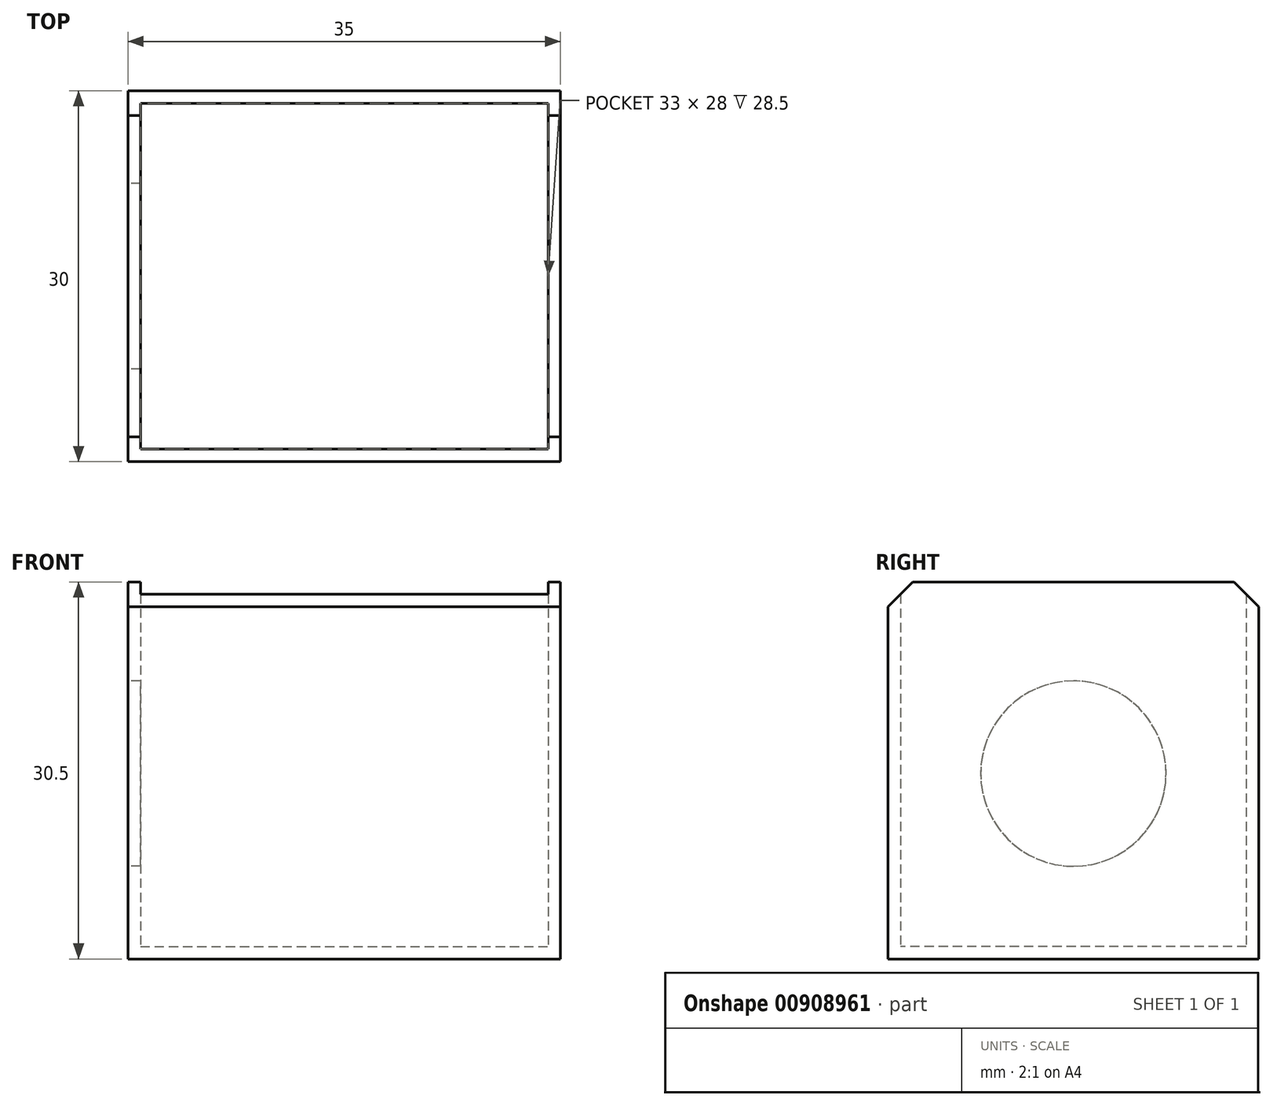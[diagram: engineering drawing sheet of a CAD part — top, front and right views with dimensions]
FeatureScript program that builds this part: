
annotation { "Feature Type Name" : "Feature", "Feature Type Description" : "" }
export const myFeature = defineFeature(function(context is Context, id is Id, definition is map)
    precondition{}
    {
        {
            var Q0;
            Q0=qCreatedBy(makeId("Top.planeOp"),FACE);
            var sketch = newSketch(context, id + "F0", { "sketchPlane" : qUnion([Q0])});
            skLineSegment(sketch, "E0", {"start": v(0, 0) * mm, "end": v(35, 0) * mm});
            skLineSegment(sketch, "E1", {"start": v(35, 0) * mm, "end": v(35, 30) * mm});
            skLineSegment(sketch, "E2", {"start": v(35, 30) * mm, "end": v(0, 30) * mm});
            skLineSegment(sketch, "E3", {"start": v(0, 30) * mm, "end": v(0, 0) * mm});
            skSolve(sketch);
        }
        {
            var Q0;
            Q0=makeQuery(id+"F0.imprint","IMPRINT",FACE,{"disambiguationData":[TD([[makeQuery(id+"F0.imprint","IMPRINT",EDGE,{"derivedFrom":sQuery(id+"F0.wireOp",EDGE,"E0")}),1.0]])]});
            extrude(context, id + "F1", {"entities" : qUnion([Q0]), "depth" : 30.5 * mm, "offsetDistance" : 25 * mm});
        }
        {
            var Q0;
            Q0=makeQuery(id+"F1.opExtrude","CAP_FACE",FACE,{"disambiguationData":[OSD([sQuery(id+"F0.wireOp",EDGE,"E0"),sQuery(id+"F0.wireOp",EDGE,"E1"),sQuery(id+"F0.wireOp",EDGE,"E2"),sQuery(id+"F0.wireOp",EDGE,"E3")])],"isStart":false});
            shell(context, id + "F2", {"entities" : qUnion([Q0]), "thickness" : 1 * mm});
        }
        {
            var Q0;
            Q0=qCreatedBy(makeId("Right.planeOp"),FACE);
            var sketch = newSketch(context, id + "F3", { "sketchPlane" : qUnion([Q0])});
            skPoint(sketch, "E4", {"position": v(15, 15) * mm});
            skSolve(sketch);
        }
        {
            var Q0;
            Q0=sQuery(id+"F3.wireOp",VERTEX,"E4");
            var Q1;
            Q1=makeQuery(id+"F1.opExtrude","SWEPT_BODY",BODY,{"disambiguationData":[OSD([sQuery(id+"F0.wireOp",EDGE,"E0"),sQuery(id+"F0.wireOp",EDGE,"E1"),sQuery(id+"F0.wireOp",EDGE,"E2"),sQuery(id+"F0.wireOp",EDGE,"E3")])]});
            hole(context, id + "F4", {"style" : HoleStyle.SIMPLE, "endStyle" : HoleEndStyle.BLIND, "oppositeDirection" : true, "holeDiameter" : 15 * mm, "majorDiameter" : 5 * mm, "holeDepth" : 12 * mm, "isTappedThrough" : true, "tappedDepth" : 12 * mm, "tapClearance" : 3, "locations" : qUnion([Q0]), "scope" : qUnion([Q1])});
        }
        {
            var Q0;
            Q0=makeQuery(id+"F1.opExtrude","CAP_EDGE",EDGE,{"disambiguationData":[OSD([sQuery(id+"F0.wireOp",EDGE,"E0")])],"isStart":false});
            chamfer(context, id + "F5", {"entities" : qUnion([Q0]), "width" : 2 * mm, "tangentPropagation" : true});
        }
        {
            var Q0;
            Q0=makeQuery(id+"F1.opExtrude","CAP_EDGE",EDGE,{"disambiguationData":[OSD([sQuery(id+"F0.wireOp",EDGE,"E2")])],"isStart":false});
            chamfer(context, id + "F6", {"entities" : qUnion([Q0]), "width" : 2 * mm, "tangentPropagation" : true});
        }
    });
